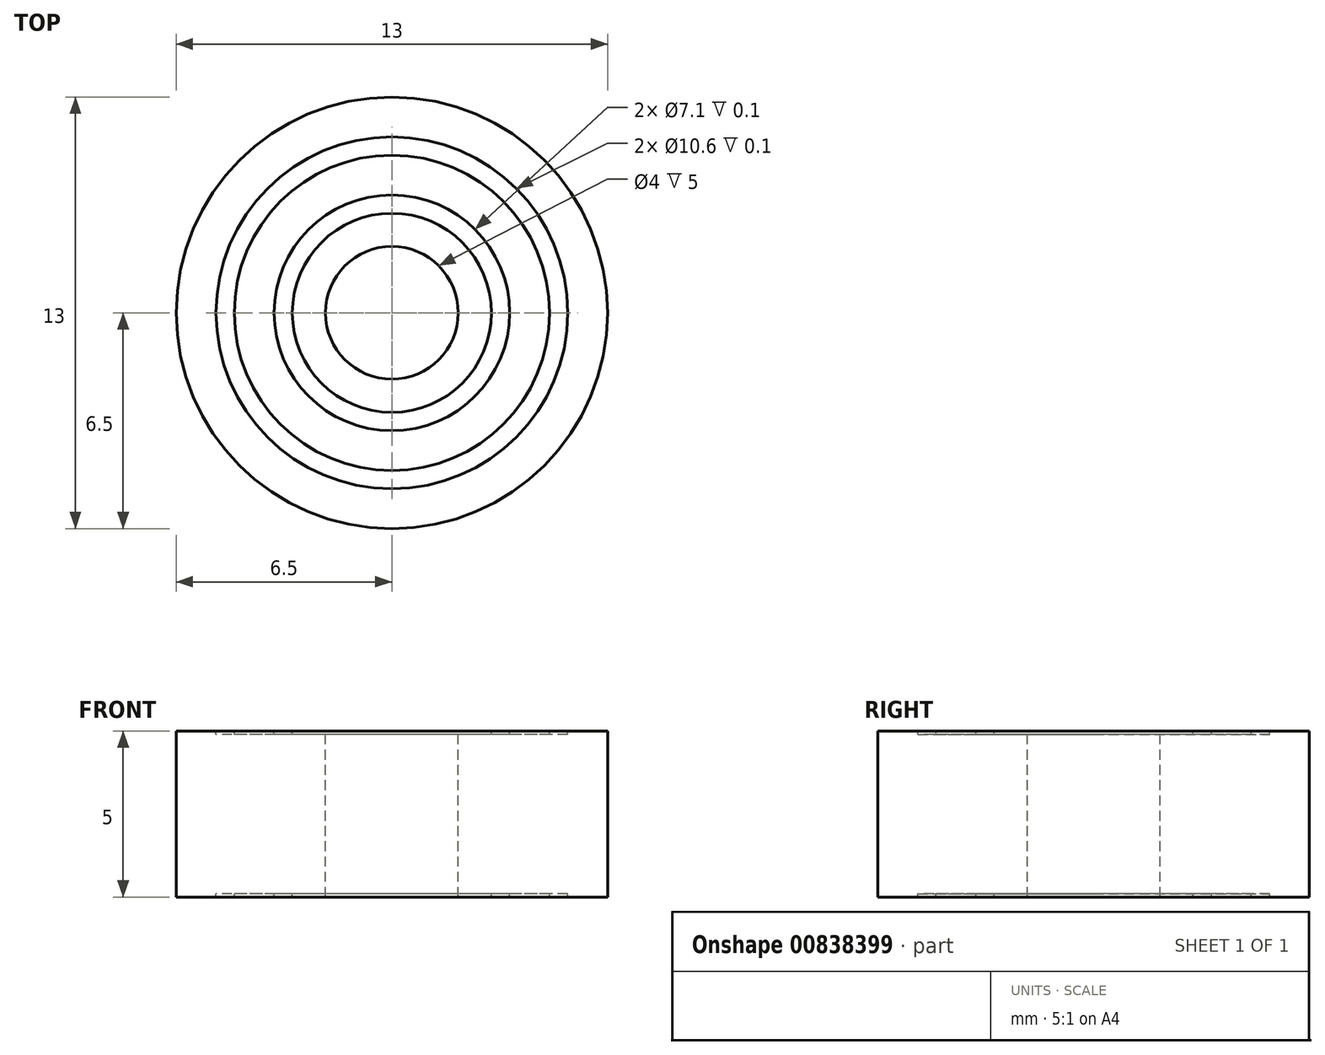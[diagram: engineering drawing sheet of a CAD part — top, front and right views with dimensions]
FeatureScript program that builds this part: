
annotation { "Feature Type Name" : "Feature", "Feature Type Description" : "" }
export const myFeature = defineFeature(function(context is Context, id is Id, definition is map)
    precondition{}
    {
        {
            var Q0;
            Q0=qCreatedBy(makeId("Front.planeOp"),FACE);
            var sketch = newSketch(context, id + "F0", { "sketchPlane" : qUnion([Q0])});
            skLineSegment(sketch, "E0", {"start": v(2, 2.5) * mm, "end": v(3, 2.5) * mm});
            skLineSegment(sketch, "E1", {"start": v(3, 2.5) * mm, "end": v(3, 2.4) * mm});
            skLineSegment(sketch, "E2", {"start": v(3, 2.4) * mm, "end": v(3.55, 2.4) * mm});
            skLineSegment(sketch, "E3", {"start": v(3.55, 2.4) * mm, "end": v(3.55, 2.5) * mm});
            skLineSegment(sketch, "E4", {"start": v(3.55, 2.5) * mm, "end": v(4.75, 2.5) * mm});
            skLineSegment(sketch, "E5", {"start": v(4.75, 2.5) * mm, "end": v(4.75, 2.4) * mm});
            skLineSegment(sketch, "E6", {"start": v(4.75, 2.4) * mm, "end": v(5.3, 2.4) * mm});
            skLineSegment(sketch, "E7", {"start": v(5.3, 2.4) * mm, "end": v(5.3, 2.5) * mm});
            skLineSegment(sketch, "E8", {"start": v(5.3, 2.5) * mm, "end": v(6.5, 2.5) * mm});
            skLineSegment(sketch, "E9", {"start": v(6.5, 2.5) * mm, "end": v(6.5, -2.5) * mm});
            skLineSegment(sketch, "E10", {"start": v(6.5, -2.5) * mm, "end": v(5.3, -2.5) * mm});
            skLineSegment(sketch, "E11", {"start": v(5.3, -2.5) * mm, "end": v(5.3, -2.4) * mm});
            skLineSegment(sketch, "E12", {"start": v(5.3, -2.4) * mm, "end": v(4.75, -2.4) * mm});
            skLineSegment(sketch, "E13", {"start": v(4.75, -2.4) * mm, "end": v(4.75, -2.5) * mm});
            skLineSegment(sketch, "E14", {"start": v(4.75, -2.5) * mm, "end": v(3.55, -2.5) * mm});
            skLineSegment(sketch, "E15", {"start": v(3.55, -2.5) * mm, "end": v(3.55, -2.4) * mm});
            skLineSegment(sketch, "E16", {"start": v(3.55, -2.4) * mm, "end": v(3, -2.4) * mm});
            skLineSegment(sketch, "E17", {"start": v(3, -2.4) * mm, "end": v(3, -2.5) * mm});
            skLineSegment(sketch, "E18", {"start": v(3, -2.5) * mm, "end": v(2, -2.5) * mm});
            skLineSegment(sketch, "E19", {"start": v(2, -2.5) * mm, "end": v(2, 2.5) * mm});
            skLineSegment(sketch, "E20", {"start": v(0, 0.76) * mm, "end": v(0, -1.2) * mm, "construction": true});
            skSolve(sketch);
        }
        {
            var Q0;
            Q0=makeQuery(id+"F0.imprint","IMPRINT",FACE,{"disambiguationData":[TD([[makeQuery(id+"F0.imprint","IMPRINT",EDGE,{"derivedFrom":sQuery(id+"F0.wireOp",EDGE,"E0")}),-1.0]])]});
            var Q1;
            Q1=sQuery(id+"F0.wireOp",EDGE,"E20");
            var Q2;
            Q2=sQuery(id+"F0.wireOp",EDGE,"E20");
            revolve(context, id + "F1", {"surfaceOperationType" : NewSurfaceOperationType.NEW, "entities" : qUnion([Q0]), "surfaceEntities" : qUnion([Q1]), "axis" : qUnion([Q2]), "revolveType" : RevolveType.FULL});
        }
    });
